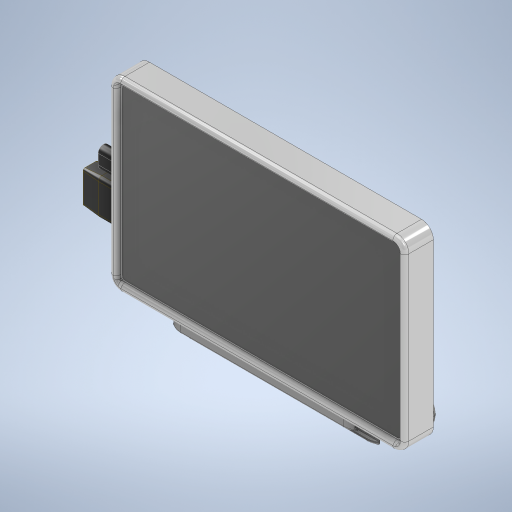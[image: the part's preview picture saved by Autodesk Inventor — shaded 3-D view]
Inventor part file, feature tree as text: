
AUTODESK INVENTOR PART (.ipt)
format: ipt  version: 2023 (Build 270158030, 158C)  size: 1,213,952 bytes
history: native  units: mm
features: extrude x26, sketch x24, fillet x22, projected_geometry x15, other x11, hole x6, chamfer x1
ambient origin geometry x8: Origin, YZ Plane, XZ Plane, XY Plane, X Axis, Y Axis, Z Axis, Center Point
bodies: Body1 (feature_tree), Body2 (feature_tree), Body3 (feature_tree), Body4 (feature_tree), Body5 (feature_tree), Body6 (feature_tree)
feature tree (105):
  other  "Monitor"
  extrude  "Extrusion1"  Depth=100.0mm
  extrude  "Extrusion2"  Depth=50.0mm
  other  "Work Point1"
  other  "Work Point2"
  other  "Work Point3"
  other  "Work Point4"
  hole  "Hole1"  [1 undecoded]
  hole  "Hole2"  [1 undecoded]
  hole  "Hole3"  [1 undecoded]
  hole  "Hole4"  [1 undecoded]
  fillet  "Fillet1"  Radius=15.0mm
  extrude  "Extrusion3"  Depth=9.15mm
  fillet  "Fillet2"  Radius=1.0mm
  extrude  "Extrusion4"  Depth=3.0mm
  extrude  "Extrusion5"  Depth=6.0mm
  fillet  "Fillet3"  Radius=8.15mm
  fillet  "Fillet4"  Radius=2.7mm
  extrude  "Extrusion6"  Depth=6.0mm
  extrude  "Extrusion7"  Depth=15.0mm
  extrude  "Extrusion8"  Depth=4.19mm
  extrude  "Extrusion9"  Depth=1.5mm
  extrude  "Extrusion10"  Depth=2.5mm
  extrude  "Extrusion11"  Depth=2.11mm
  fillet  "Fillet5"  Radius=0.45mm
  fillet  "Fillet6"  Radius=0.45mm
  extrude  "Extrusion22"  Depth=0.45mm
  other  "Work Point5"
  extrude  "Extrusion23"  Depth=0.45mm
  fillet  "Fillet22"  Radius=0.4mm
  extrude  "Extrusion24"  Depth=0.2mm
  extrude  "Extrusion25"  Depth=12.0mm TaperAngle=0.0deg
  extrude  "Extrusion26"  Depth=3.0mm
  extrude  "Extrusion12"  Depth=3.0mm
  extrude  "Extrusion13"  Depth=3.0mm
  sketch  "Sketch15"  dims[d58=3.0mm d59=0.0mm d60=15.0mm]
  hole  "Hole6"  [1 undecoded]
  fillet  "Fillet7"  Radius=7.5mm
  extrude  "Extrusion14"  Depth=2.0mm TaperAngle=0.0deg
  chamfer  "Chamfer1"  Distance=4.9mm
  fillet  "Fillet8"  Radius=0.73mm
  fillet  "Fillet20"  Radius=2.55mm
  fillet  "Fillet9"  Radius=39.0mm
  extrude  "Extrusion15"  Depth=3.0mm TaperAngle=0.0deg
  extrude  "Extrusion16"  Depth=3.0mm
  fillet  "Fillet10"  Radius=3.175mm
  fillet  "Fillet11"  Radius=5.0mm
  extrude  "Extrusion17"  Depth=3.0mm TaperAngle=0.0deg
  extrude  "Extrusion18"  Depth=3.0mm
  extrude  "Extrusion19"  Depth=3.0mm
  hole  "Hole7"  [1 undecoded]
  fillet  "Fillet12"  Radius=18.6mm
  extrude  "Extrusion20"  Depth=3.0mm
  extrude  "Extrusion21"  Depth=3.0mm
  fillet  "Fillet14"  Radius=5.09mm
  fillet  "Fillet15"  Radius=3.0mm
  fillet  "Fillet16"  Radius=0.2mm
  fillet  "Fillet17"  Radius=5.0mm
  fillet  "Fillet18"  Radius=5.0mm
  fillet  "Fillet19"  Radius=5.0mm
  fillet  "Fillet21"  Radius=5.0mm
  fillet  "Fillet23"  Radius=12.0mm
  sketch  "Sketch1"  dims[d0=165.0mm d1=100.0mm]
  sketch  "Sketch2"  dims[d2=82.5mm d3=50.0mm]
  sketch  "Sketch4"  dims[d4=8.36mm d5=0.0mm d6=5.5mm]
  sketch  "Sketch5"  dims[d7=5.0mm d8=5.0mm]
  projected_geometry  "Projected Loop1"
  sketch  "Sketch6"  dims[d9=5.0mm d10=5.0mm]
  sketch  "Sketch7"  dims[d11=4.0mm d12=0.0mm]
  projected_geometry  "Projected Loop2"
  sketch  "Sketch8"  dims[d42=10.0mm d43=10.0mm d15=2.013mm d16=4.0mm d17=4.0mm d18=2.0mm d19=90.0deg d20=4.0mm d21=20.594885mm]
  sketch  "Sketch9"  dims[d24=10.0mm d25=10.0mm d26=2.013mm d27=4.0mm d28=4.0mm d29=2.0mm d30=90.0deg d31=4.0mm d32=20.594885mm]
  projected_geometry  "Projected Loop3"
  sketch  "Sketch10"  dims[d33=10.0mm d34=10.0mm d35=2.013mm d36=4.0mm d37=4.0mm d38=2.0mm d39=90.0deg d40=4.0mm d41=20.594885mm]
  sketch  "Sketch11"  dims[d44=10.0mm d45=10.0mm d46=2.013mm d47=4.0mm d48=4.0mm d49=2.0mm d50=90.0deg d51=4.0mm d52=20.594885mm d53=2.0mm d54=15.0mm]
  sketch  "Sketch12"  dims[d55=12.0mm d56=9.15mm d57=1.0mm]
  other  "case"
  projected_geometry  "Projected Loop4"
  projected_geometry  "Projected Loop5"
  projected_geometry  "Projected Loop6"
  sketch  "Sketch16"  dims[d61=12.0mm d62=6.0mm d63=8.15mm d64=4.075mm d65=2.7mm d66=0.0mm]
  projected_geometry  "Projected Loop7"
  sketch  "Sketch17"  dims[d67=6.0mm d68=0.5mm]
  projected_geometry  "Projected Loop8"
  projected_geometry  "Projected Loop9"
  projected_geometry  "Projected Loop10"
  other  "screws"
  sketch  "Sketch18"  dims[d69=0.5mm d70=15.0mm]
  sketch  "Sketch19"  dims[d71=6.3mm d72=4.19mm d73=0.7mm]
  sketch  "Sketch20"  dims[d74=1.5mm d75=1.5mm]
  other  "clip"
  sketch  "Sketch22"  dims[d76=20.5mm d77=2.5mm]
  projected_geometry  "Projected Loop11"
  sketch  "Sketch23"  dims[d78=2.5mm d79=2.11mm d80=0.45mm d81=0.45mm]
  sketch  "Sketch26"  dims[d82=0.45mm d83=0.45mm]
  projected_geometry  "Projected Loop12"
  other  "HDMI"
  sketch  "Sketch27"  dims[d84=0.45mm d85=0.45mm d86=0.4mm d87=0.0mm]
  sketch  "Sketch28"  dims[d88=0.5mm d89=0.2mm]
  projected_geometry  "Projected Loop13"
  sketch  "Sketch29"  dims[d90=4.5mm d91=0.0mm d92=12.0mm d93=0.0mm]
  projected_geometry  "Projected Loop14"
  other  "USB-C"
  sketch  "Sketch30"  dims[d94=9.1mm d95=3.2mm d96=0.1mm d97=43.0mm d98=0.35mm d99=7.5mm d100=0.0mm d101=2.0mm d102=0.0mm d103=4.9mm d104=0.73mm d105=2.55mm d106=39.0mm d107=14.0mm d108=0.0mm d109=6.35mm d110=3.175mm d111=5.0mm d112=12.0mm d113=0.0mm d114=38.0mm d115=18.0mm d116=38.0mm d117=18.6mm d118=7.67mm d119=21.67mm d120=5.09mm d121=0.0mm d122=3.0mm d123=0.2mm d124=5.0mm d125=5.0mm d126=5.0mm d127=5.0mm d128=12.0mm d130=12.0mm d132=2.0mm d133=0.0mm d134=16.0mm d135=19.0mm d136=2.0mm d139=2.0mm d141=2.0mm d143=2.0mm d145=2.0mm d146=2.0mm d147=5.0mm d148=0.7mm d149=8.0mm d150=8.0mm d151=0.7mm d152=0.7mm d154=15.0mm d155=0.0mm d167=2.9mm d168=6.0mm d169=5.5mm d170=0.5mm d171=90.0deg d172=7.6mm d173=20.594885mm d174=7.0mm d175=16.0mm d176=10.0mm d177=10.0mm d178=4.6mm d179=73.5mm d180=0.0mm d181=2.0mm d182=2.0mm d183=45.0deg d184=2.5mm d185=3.0mm d186=7.3mm d187=2.0mm d188=0.0mm d189=0.0mm d190=4.16mm d191=1.4mm d192=0.0mm d193=0.6mm d194=4.0mm d195=1.4mm d196=0.0mm d197=4.0mm d198=5.0mm d199=5.0mm d200=6.0mm d201=3.0mm d202=3.0mm d203=0.0mm d204=15.0mm d205=15.0mm d206=4.5mm d207=0.0mm d208=2.9mm d209=6.0mm d210=5.5mm d211=2.0mm d212=90.0deg d213=7.6mm d214=20.594885mm d215=10.0mm d216=24.180074mm d217=24.180074mm d218=14.0mm d219=0.0mm d221=0.7mm d223=1.5mm d225=10.0mm d227=1.5mm d228=2.0mm d229=1.9mm d230=1.5mm d231=14.0mm d232=0.0mm d233=10.0mm d234=2.0mm d235=1.0mm d236=1.0mm d237=1.5mm d238=10.0mm d240=0.7mm d241=0.7mm d242=0.5mm d244=24.180074mm d245=1.65mm d246=11.165mm d247=3.0mm d248=2.45mm d249=2.45mm d250=0.0mm d251=0.0mm d252=21.0mm d253=10.5mm d254=2.9mm d255=2.9mm d256=3.45mm d257=3.45mm d258=17.6mm d259=0.0mm d260=2.0mm d261=10.0mm d262=-0.872665mm d263=2.4mm d264=2.4mm d265=0.0mm d266=0.0mm d267=6.2mm d268=12.1mm d269=18.6mm d270=0.0mm d271=0.5mm d272=3.0mm]
  projected_geometry  "Projected Loop15"
note: 6 required parameter values undecoded (feature->parameter linkage not recoverable at this tier; creation-order binding heuristic only, values carry confidence <= 0.55)
